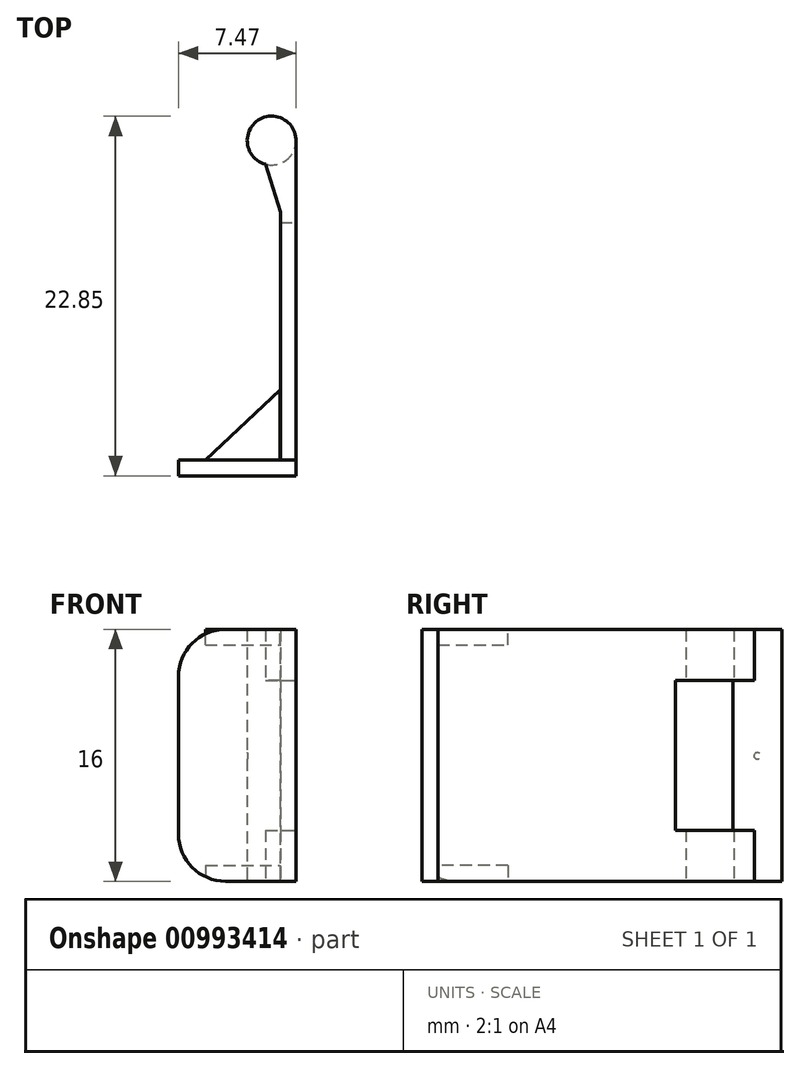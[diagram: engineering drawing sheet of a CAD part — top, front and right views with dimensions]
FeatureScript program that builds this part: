
annotation { "Feature Type Name" : "Feature", "Feature Type Description" : "" }
export const myFeature = defineFeature(function(context is Context, id is Id, definition is map)
    precondition{}
    {
        {
            var Q0;
            Q0=qCreatedBy(makeId("Top.planeOp"),FACE);
            var sketch = newSketch(context, id + "F0", { "sketchPlane" : qUnion([Q0])});
            skLineSegment(sketch, "E0", {"start": v(-7.47, 0) * mm, "end": v(0, 0) * mm});
            skLineSegment(sketch, "E1", {"start": v(0, 0) * mm, "end": v(0, 20.1) * mm});
            skSolve(sketch);
        }
        {
            var Q0;
            Q0=sQuery(id+"F0.wireOp",EDGE,"E1");
            var Q1;
            Q1=sQuery(id+"F0.wireOp",EDGE,"E0");
            extrude(context, id + "F1", {"bodyType" : ToolBodyType.SURFACE, "surfaceEntities" : qUnion([Q0, Q1]), "depth" : 16 * mm, "offsetDistance" : 25 * mm});
        }
        {
            var Q0;
            Q0=makeQuery(id+"F1.opExtrude","SWEPT_FACE",FACE,{"disambiguationData":[OSD([sQuery(id+"F0.wireOp",EDGE,"E1")])]});
            extrude(context, id + "F2", {"entities" : qUnion([Q0]), "oppositeDirection" : true, "depth" : 1 * mm, "offsetDistance" : 25 * mm});
        }
        {
            var Q0;
            Q0=makeQuery(id+"F1.opExtrude","SWEPT_FACE",FACE,{"disambiguationData":[OSD([sQuery(id+"F0.wireOp",EDGE,"E0")])]});
            extrude(context, id + "F3", {"entities" : qUnion([Q0]), "depth" : 1 * mm, "offsetDistance" : 25 * mm});
        }
        {
            var Q0;
            Q0=makeQuery(id+"F1.opExtrude","SWEPT_FACE",FACE,{"disambiguationData":[OSD([sQuery(id+"F0.wireOp",EDGE,"E1")])]});
            var sketch = newSketch(context, id + "F4", { "sketchPlane" : qUnion([Q0])});
            skLineSegment(sketch, "E2.bottom", {"start": v(20.1, 12.75) * mm, "end": v(15.1, 12.75) * mm});
            skLineSegment(sketch, "E2.top", {"start": v(20.1, 3.25) * mm, "end": v(15.1, 3.25) * mm});
            skLineSegment(sketch, "E2.left", {"start": v(20.1, 12.75) * mm, "end": v(20.1, 3.25) * mm});
            skLineSegment(sketch, "E2.right", {"start": v(15.1, 12.75) * mm, "end": v(15.1, 3.25) * mm});
            skSolve(sketch);
        }
        {
            var Q0;
            Q0=qSketchRegion(id+"F4",true);
            extrude(context, id + "F5", {"entities" : qUnion([Q0]), "operationType" : NewBodyOperationType.REMOVE, "endBound" : BoundingType.SYMMETRIC, "oppositeDirection" : true, "depth" : 5 * mm, "offsetDistance" : 25 * mm});
        }
        {
            var Q0;
            {var subQ0=sQuery(id+"F0.wireOp",EDGE,"E1");Q0=makeQuery(id+"F2.opExtrude","SWEPT_FACE",FACE,{"disambiguationData":[OSD([subQ0]),TDD([makeQuery(id+"F1.opExtrude","CAP_EDGE",EDGE,{"disambiguationData":[OSD([subQ0])],"isStart":true})])]});}
            var sketch = newSketch(context, id + "F6", { "sketchPlane" : qUnion([Q0])});
            skCircle(sketch, "E3", {"center": v(-1.55, -20.3) * mm, "radius": 1.55 * mm});
            skSolve(sketch);
        }
        {
            var Q0;
            Q0=qSketchRegion(id+"F6",true);
            extrude(context, id + "F7", {"entities" : qUnion([Q0]), "operationType" : NewBodyOperationType.ADD, "oppositeDirection" : true, "depth" : 16 * mm, "offsetDistance" : 25 * mm});
        }
        {
            var Q0;
            {var subQ0=sQuery(id+"F0.wireOp",EDGE,"E1");Q0=makeQuery(id+"F7.boolean.opBoolean","MERGE",FACE,{"derivedFrom":[makeQuery(id+"F2.opExtrude","SWEPT_FACE",FACE,{"disambiguationData":[OSD([subQ0]),TDD([makeQuery(id+"F1.opExtrude","CAP_EDGE",EDGE,{"disambiguationData":[OSD([subQ0])],"isStart":true})])]}),makeQuery(id+"F7.opExtrude","CAP_FACE",FACE,{"disambiguationData":[OSD([sQuery(id+"F6.wireOp",EDGE,"E3")])],"isStart":true})]});}
            var sketch = newSketch(context, id + "F8", { "sketchPlane" : qUnion([Q0])});
            skLineSegment(sketch, "E4", {"start": v(-5.75, 0) * mm, "end": v(-1.01, 0) * mm});
            skLineSegment(sketch, "E5.MirrorCS", {"start": v(-1.01, -4.46) * mm, "end": v(-5.75, 0) * mm});
            skLineSegment(sketch, "E6.MirrorCS", {"start": v(-1.01, 0) * mm, "end": v(-1.01, -4.46) * mm});
            skSolve(sketch);
        }
        {
            var Q0;
            Q0=qSketchRegion(id+"F8",true);
            extrude(context, id + "F9", {"entities" : qUnion([Q0]), "operationType" : NewBodyOperationType.ADD, "oppositeDirection" : true, "depth" : 1 * mm, "offsetDistance" : 25 * mm});
        }
        {
            var Q0;
            {var subQ0=sQuery(id+"F0.wireOp",EDGE,"E0");Q0=makeQuery(id+"F3.opExtrude","SWEPT_FACE",FACE,{"disambiguationData":[OSD([subQ0]),TDD([makeQuery(id+"F1.opExtrude","CAP_EDGE",EDGE,{"disambiguationData":[OSD([subQ0])],"isStart":false})])]});}
            var sketch = newSketch(context, id + "F10", { "sketchPlane" : qUnion([Q0])});
            skLineSegment(sketch, "E7", {"start": v(-1.02, 0) * mm, "end": v(-1.02, 4.46) * mm});
            skLineSegment(sketch, "E8", {"start": v(-1.02, 4.46) * mm, "end": v(-5.75, 0) * mm});
            skLineSegment(sketch, "E9", {"start": v(-5.75, 0) * mm, "end": v(-1.02, 0) * mm});
            skSolve(sketch);
        }
        {
            var Q0;
            Q0=qSketchRegion(id+"F10",true);
            extrude(context, id + "F11", {"entities" : qUnion([Q0]), "oppositeDirection" : true, "depth" : 1 * mm, "offsetDistance" : 25 * mm});
        }
        {
            var Q0;
            {var subQ0=sQuery(id+"F0.wireOp",VERTEX,"E0.start");Q0=makeQuery(id+"F3.opExtrude","SWEPT_EDGE",EDGE,{"disambiguationData":[OSD([subQ0]),TDD([makeQuery(id+"F1.opExtrude","CAP_VERTEX",VERTEX,{"disambiguationData":[OSD([subQ0])],"isStart":true})])]});}
            var Q1;
            {var subQ0=sQuery(id+"F0.wireOp",VERTEX,"E0.start");Q1=makeQuery(id+"F3.opExtrude","SWEPT_EDGE",EDGE,{"disambiguationData":[OSD([subQ0]),TDD([makeQuery(id+"F1.opExtrude","CAP_VERTEX",VERTEX,{"disambiguationData":[OSD([subQ0])],"isStart":false})])]});}
            fillet(context, id + "F12", {"entities" : qUnion([Q0, Q1]), "radius" : 3 * mm, "tangentPropagation" : true, "allowEdgeOverflow" : false});
        }
        {
            var Q0;
            Q0=makeQuery(id+"F7.boolean.opBoolean","INTERSECT",EDGE,{"disambiguationData":[OD(0.0)],"derivedFrom":[makeQuery(id+"F2.opExtrude","CAP_FACE",FACE,{"disambiguationData":[OSD([sQuery(id+"F0.wireOp",EDGE,"E1")])],"isStart":false}),makeQuery(id+"F7.opExtrude","SWEPT_FACE",FACE,{"disambiguationData":[OSD([sQuery(id+"F6.wireOp",EDGE,"E3")])]})]});
            var Q1;
            Q1=makeQuery(id+"F7.boolean.opBoolean","INTERSECT",EDGE,{"disambiguationData":[OD(1.0)],"derivedFrom":[makeQuery(id+"F2.opExtrude","CAP_FACE",FACE,{"disambiguationData":[OSD([sQuery(id+"F0.wireOp",EDGE,"E1")])],"isStart":false}),makeQuery(id+"F7.opExtrude","SWEPT_FACE",FACE,{"disambiguationData":[OSD([sQuery(id+"F6.wireOp",EDGE,"E3")])]})]});
            chamfer(context, id + "F13", {"entities" : qUnion([Q0, Q1]), "chamferType" : ChamferType.OFFSET_ANGLE, "width" : 4 * mm, "oppositeDirection" : false, "angle" : 44 * degree, "tangentPropagation" : true});
        }
        {
            var Q0;
            Q0=makeQuery(id+"F3.opExtrude","CAP_FACE",FACE,{"disambiguationData":[OSD([sQuery(id+"F0.wireOp",EDGE,"E0")])],"isStart":false});
            var sketch = newSketch(context, id + "F14", { "sketchPlane" : qUnion([Q0])});
            skPoint(sketch, "E10", {"position": v(-4.33, 7.97) * mm});
            skSolve(sketch);
        }
        {
            var Q0;
            Q0=sQuery(id+"F14.wireOp",VERTEX,"E10");
            var Q1;
            Q1=makeQuery(id+"F2.opExtrude","SWEPT_BODY",BODY,{"disambiguationData":[OSD([sQuery(id+"F0.wireOp",EDGE,"E1")])]});
            hole(context, id + "F15", {"style" : HoleStyle.SIMPLE, "endStyle" : HoleEndStyle.THROUGH, "holeDiameter" : 2.5 * mm, "majorDiameter" : 5 * mm, "isTappedThrough" : true, "tappedDepth" : 12 * mm, "tapClearance" : 3, "locations" : qUnion([Q0]), "scope" : qUnion([Q1])});
        }
    });
